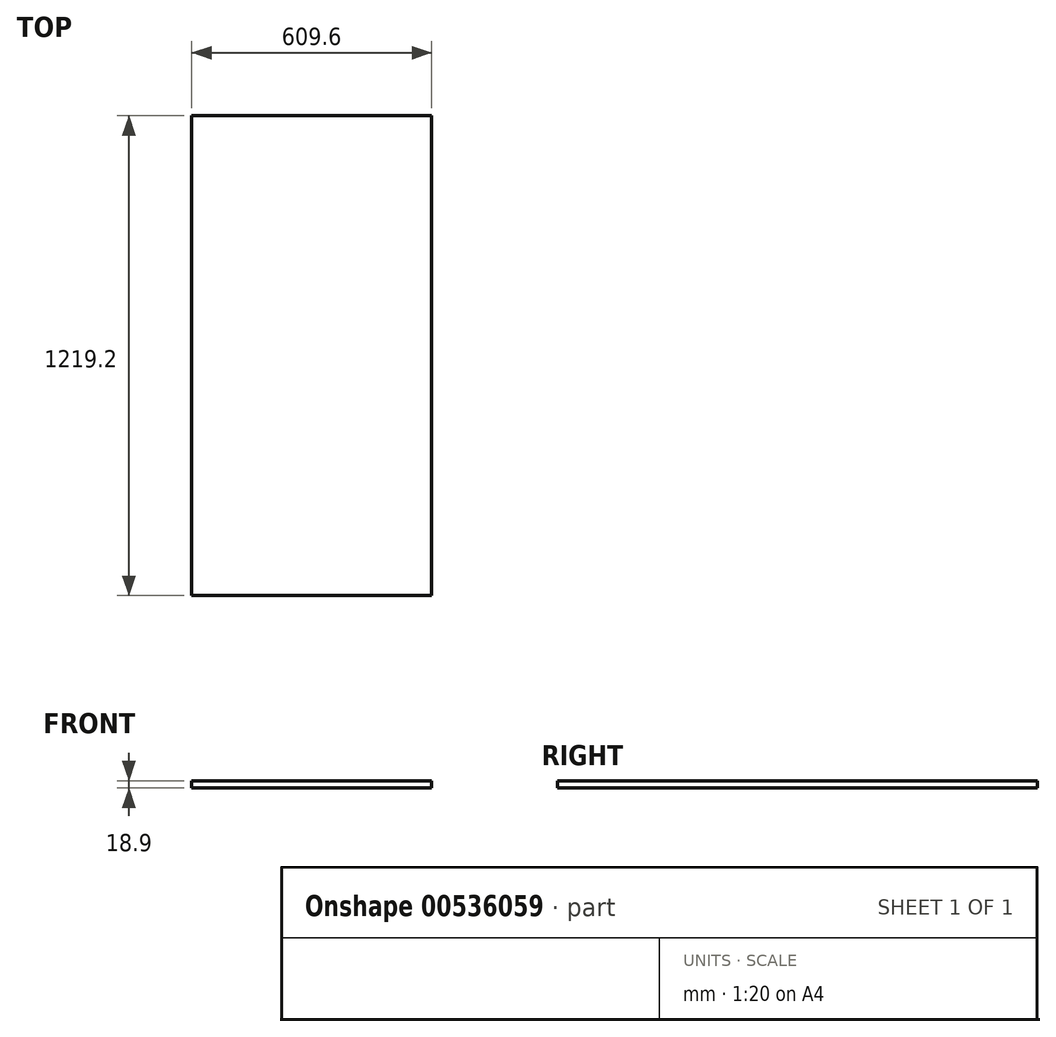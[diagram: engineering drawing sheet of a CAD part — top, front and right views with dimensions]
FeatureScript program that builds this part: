
annotation { "Feature Type Name" : "Feature", "Feature Type Description" : "" }
export const myFeature = defineFeature(function(context is Context, id is Id, definition is map)
    precondition{}
    {
        {
            var Q0;
            Q0=qCreatedBy(makeId("Top.planeOp"),FACE);
            var sketch = newSketch(context, id + "F0", { "sketchPlane" : qUnion([Q0])});
            skLineSegment(sketch, "E0.bottom", {"start": v(0, 0) * mm, "end": v(609.6, 0) * mm});
            skLineSegment(sketch, "E0.top", {"start": v(0, 1219.2) * mm, "end": v(609.6, 1219.2) * mm});
            skLineSegment(sketch, "E0.left", {"start": v(0, 0) * mm, "end": v(0, 1219.2) * mm});
            skLineSegment(sketch, "E0.right", {"start": v(609.6, 0) * mm, "end": v(609.6, 1219.2) * mm});
            skSolve(sketch);
        }
        {
            var Q0;
            Q0=makeQuery(id+"F0.imprint","IMPRINT",FACE,{"disambiguationData":[TD([[makeQuery(id+"F0.imprint","IMPRINT",EDGE,{"derivedFrom":sQuery(id+"F0.wireOp",EDGE,"E0.bottom")}),1.0]])]});
            extrude(context, id + "F1", {"entities" : qUnion([Q0]), "depth" : 18.9 * mm, "offsetDistance" : 30.48 * mm});
        }
    });
